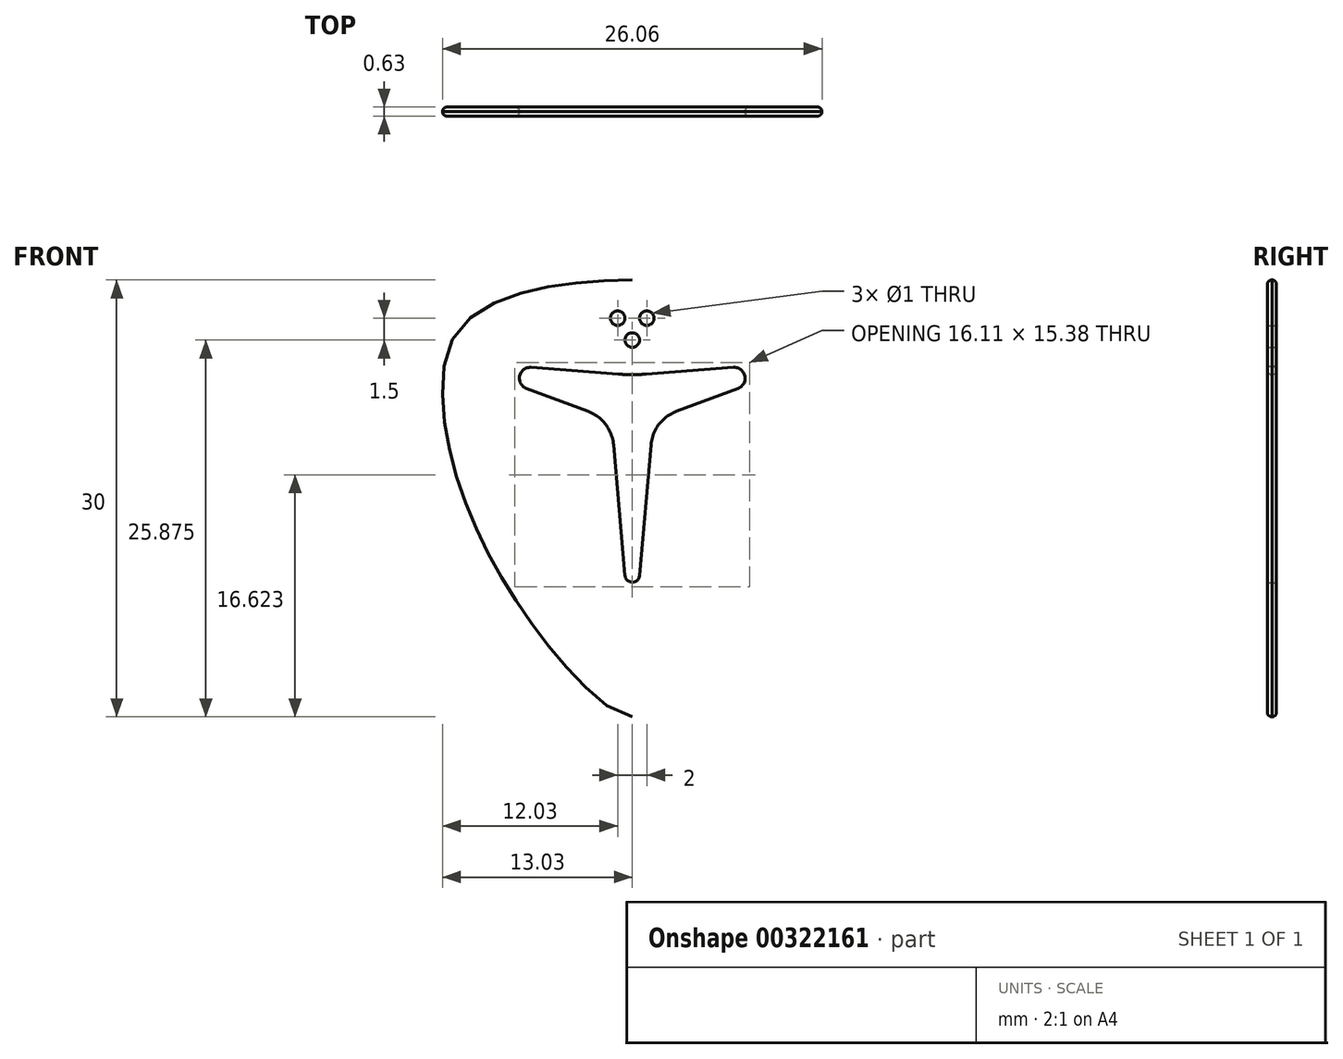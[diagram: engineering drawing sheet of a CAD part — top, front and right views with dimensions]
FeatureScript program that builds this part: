
annotation { "Feature Type Name" : "Feature", "Feature Type Description" : "" }
export const myFeature = defineFeature(function(context is Context, id is Id, definition is map)
    precondition{}
    {
        {
            var Q0;
            Q0=qCreatedBy(makeId("Front.planeOp"),FACE);
            var sketch = newSketch(context, id + "F0", { "sketchPlane" : qUnion([Q0])});
            skLineSegment(sketch, "E0", {"start": v(0, 0) * mm, "end": v(0, 6.75) * mm, "construction": true});
            skLineSegment(sketch, "E1", {"start": v(0, 0) * mm, "end": v(0, -23.25) * mm, "construction": true});
            skLineSegment(sketch, "E2", {"start": v(0, 0) * mm, "end": v(13, 0) * mm, "construction": true});
            skFitSpline(sketch, "E3", {"points": [v(0, -23.25) * mm, v(9.5, -12.75) * mm, v(13, 0) * mm, v(11, 4.25) * mm, v(0, 6.75) * mm], "startDerivative": vector(20.6, 0) * mm, "endDerivative": vector(-57.72, 0) * mm});
            skFitSpline(sketch, "E4.MirrorCS", {"points": [v(0, -23.25) * mm, v(-9.5, -12.75) * mm, v(-13, 0) * mm, v(-11, 4.25) * mm, v(0, 6.75) * mm], "startDerivative": vector(-20.6, 0) * mm, "endDerivative": vector(57.72, 0) * mm});
            skArc(sketch, "E5", {"start": v(7.26, -0.7) * mm, "mid": v(7.73, 0.16) * mm, "end": v(6.94, 0.75) * mm});
            skLineSegment(sketch, "E6", {"start": v(7.26, -0.7) * mm, "end": v(3.04, -2.27) * mm});
            skArc(sketch, "E7", {"start": v(3.04, -2.27) * mm, "mid": v(1.83, -3.17) * mm, "end": v(1.28, -4.58) * mm});
            skLineSegment(sketch, "E8", {"start": v(0.5, -13.54) * mm, "end": v(1.28, -4.58) * mm});
            skArc(sketch, "E9", {"start": v(0, -14) * mm, "mid": v(0.34, -13.87) * mm, "end": v(0.5, -13.54) * mm});
            skArc(sketch, "E10.MirrorCS", {"start": v(0, -14) * mm, "mid": v(-0.34, -13.87) * mm, "end": v(-0.5, -13.54) * mm});
            skLineSegment(sketch, "E11.MirrorCS", {"start": v(-0.5, -13.54) * mm, "end": v(-1.28, -4.58) * mm});
            skArc(sketch, "E12.MirrorCS", {"start": v(-3.04, -2.27) * mm, "mid": v(-1.83, -3.17) * mm, "end": v(-1.28, -4.58) * mm});
            skLineSegment(sketch, "E13.MirrorCS", {"start": v(-7.26, -0.7) * mm, "end": v(-3.04, -2.27) * mm});
            skArc(sketch, "E14.MirrorCS", {"start": v(-7.26, -0.7) * mm, "mid": v(-7.73, 0.16) * mm, "end": v(-6.94, 0.75) * mm});
            skLineSegment(sketch, "E15", {"start": v(6.94, 0.75) * mm, "end": v(0.96, 0.29) * mm});
            skArc(sketch, "E16", {"start": v(0, 0.25) * mm, "mid": v(0.48, 0.26) * mm, "end": v(0.96, 0.29) * mm});
            skArc(sketch, "E17.MirrorCS", {"start": v(0, 0.25) * mm, "mid": v(-0.48, 0.26) * mm, "end": v(-0.96, 0.29) * mm});
            skLineSegment(sketch, "E18.MirrorCS", {"start": v(-6.94, 0.75) * mm, "end": v(-0.96, 0.29) * mm});
            skLineSegment(sketch, "E19", {"start": v(0, 4.12) * mm, "end": v(1, 4.12) * mm});
            skCircle(sketch, "E20", {"center": v(1, 4.12) * mm, "radius": 0.5 * mm});
            skCircle(sketch, "E21", {"center": v(0, 2.62) * mm, "radius": 0.5 * mm});
            skPoint(sketch, "E22", {"position": v(0, 3.38) * mm});
            skLineSegment(sketch, "E23.MirrorCS", {"start": v(0, 4.12) * mm, "end": v(-1, 4.12) * mm});
            skCircle(sketch, "E24.MirrorC", {"center": v(-1, 4.12) * mm, "radius": 0.5 * mm});
            skSolve(sketch);
        }
        {
            var Q0;
            Q0=qSketchRegion(id+"F0",true);
            extrude(context, id + "F1", {"entities" : qUnion([Q0]), "depth" : 0.63 * mm});
        }
        {
            var Q0;
            Q0=makeQuery(id+"F1.opExtrude","CAP_EDGE",EDGE,{"disambiguationData":[OSD([sQuery(id+"F0.wireOp",EDGE,"E5")])],"isStart":false});
            var Q1;
            Q1=makeQuery(id+"F1.opExtrude","CAP_EDGE",EDGE,{"disambiguationData":[OSD([sQuery(id+"F0.wireOp",EDGE,"E7")])],"isStart":true});
            var Q2;
            Q2=makeQuery(id+"F1.opExtrude","CAP_EDGE",EDGE,{"disambiguationData":[OSD([sQuery(id+"F0.wireOp",EDGE,"E9"),sQuery(id+"F0.wireOp",EDGE,"E10.MirrorCS")])],"isStart":false});
            var Q3;
            Q3=makeQuery(id+"F1.opExtrude","CAP_EDGE",EDGE,{"disambiguationData":[OSD([sQuery(id+"F0.wireOp",EDGE,"E14.MirrorCS")])],"isStart":false});
            var Q4;
            Q4=makeQuery(id+"F1.opExtrude","CAP_EDGE",EDGE,{"disambiguationData":[OSD([sQuery(id+"F0.wireOp",EDGE,"E5")])],"isStart":true});
            var Q5;
            Q5=makeQuery(id+"F1.opExtrude","CAP_EDGE",EDGE,{"disambiguationData":[OSD([sQuery(id+"F0.wireOp",EDGE,"E12.MirrorCS")])],"isStart":false});
            var Q6;
            Q6=makeQuery(id+"F1.opExtrude","CAP_EDGE",EDGE,{"disambiguationData":[OSD([sQuery(id+"F0.wireOp",EDGE,"E7")])],"isStart":false});
            var Q7;
            Q7=makeQuery(id+"F1.opExtrude","CAP_EDGE",EDGE,{"disambiguationData":[OSD([sQuery(id+"F0.wireOp",EDGE,"cP70XH3B-hxny-nh1n-TbyW-52Zl4TOD4HrO"),sQuery(id+"F0.wireOp",EDGE,"9cf6c757-e815-40dd-95a7-672993b90d513.MirrorCS")])],"isStart":true});
            var Q8;
            Q8=makeQuery(id+"F1.opExtrude","CAP_EDGE",EDGE,{"disambiguationData":[OSD([sQuery(id+"F0.wireOp",EDGE,"E13.MirrorCS")])],"isStart":false});
            var Q9;
            Q9=makeQuery(id+"F1.opExtrude","CAP_EDGE",EDGE,{"disambiguationData":[OSD([sQuery(id+"F0.wireOp",EDGE,"E12.MirrorCS")])],"isStart":true});
            var Q10;
            Q10=makeQuery(id+"F1.opExtrude","CAP_EDGE",EDGE,{"disambiguationData":[OSD([sQuery(id+"F0.wireOp",EDGE,"cP70XH3B-hxny-nh1n-TbyW-52Zl4TOD4HrO"),sQuery(id+"F0.wireOp",EDGE,"9cf6c757-e815-40dd-95a7-672993b90d513.MirrorCS")])],"isStart":false});
            var Q11;
            Q11=makeQuery(id+"F1.opExtrude","CAP_EDGE",EDGE,{"disambiguationData":[OSD([sQuery(id+"F0.wireOp",EDGE,"E9"),sQuery(id+"F0.wireOp",EDGE,"E10.MirrorCS")])],"isStart":true});
            var Q12;
            Q12=makeQuery(id+"F1.opExtrude","SWEPT_EDGE",EDGE,{"disambiguationData":[OSD([sQuery(id+"F0.wireOp",EDGE,"9cf6c757-e815-40dd-95a7-672993b90d513.MirrorCS"),sQuery(id+"F0.wireOp",EDGE,"E14.MirrorCS")])]});
            var Q13;
            Q13=makeQuery(id+"F1.opExtrude","CAP_EDGE",EDGE,{"disambiguationData":[OSD([sQuery(id+"F0.wireOp",EDGE,"E8")])],"isStart":true});
            var Q14;
            Q14=makeQuery(id+"F1.opExtrude","CAP_EDGE",EDGE,{"disambiguationData":[OSD([sQuery(id+"F0.wireOp",EDGE,"E11.MirrorCS")])],"isStart":false});
            var Q15;
            Q15=makeQuery(id+"F1.opExtrude","SWEPT_EDGE",EDGE,{"disambiguationData":[OSD([sQuery(id+"F0.wireOp",EDGE,"E6"),sQuery(id+"F0.wireOp",EDGE,"E7")])]});
            var Q16;
            Q16=makeQuery(id+"F1.opExtrude","SWEPT_EDGE",EDGE,{"disambiguationData":[OSD([sQuery(id+"F0.wireOp",EDGE,"E8"),sQuery(id+"F0.wireOp",EDGE,"E9")])]});
            var Q17;
            Q17=makeQuery(id+"F1.opExtrude","SWEPT_EDGE",EDGE,{"disambiguationData":[OSD([sQuery(id+"F0.wireOp",EDGE,"E13.MirrorCS"),sQuery(id+"F0.wireOp",EDGE,"E14.MirrorCS")])]});
            var Q18;
            Q18=makeQuery(id+"F1.opExtrude","SWEPT_EDGE",EDGE,{"disambiguationData":[OSD([sQuery(id+"F0.wireOp",EDGE,"E10.MirrorCS"),sQuery(id+"F0.wireOp",EDGE,"E11.MirrorCS")])]});
            var Q19;
            Q19=makeQuery(id+"F1.opExtrude","SWEPT_EDGE",EDGE,{"disambiguationData":[OSD([sQuery(id+"F0.wireOp",EDGE,"E11.MirrorCS"),sQuery(id+"F0.wireOp",EDGE,"E12.MirrorCS")])]});
            var Q20;
            Q20=makeQuery(id+"F1.opExtrude","SWEPT_EDGE",EDGE,{"disambiguationData":[OSD([sQuery(id+"F0.wireOp",EDGE,"E5"),sQuery(id+"F0.wireOp",EDGE,"E6")])]});
            var Q21;
            Q21=makeQuery(id+"F1.opExtrude","CAP_EDGE",EDGE,{"disambiguationData":[OSD([sQuery(id+"F0.wireOp",EDGE,"E14.MirrorCS")])],"isStart":true});
            var Q22;
            Q22=makeQuery(id+"F1.opExtrude","SWEPT_EDGE",EDGE,{"disambiguationData":[OSD([sQuery(id+"F0.wireOp",EDGE,"E12.MirrorCS"),sQuery(id+"F0.wireOp",EDGE,"E13.MirrorCS")])]});
            var Q23;
            Q23=makeQuery(id+"F1.opExtrude","CAP_EDGE",EDGE,{"disambiguationData":[OSD([sQuery(id+"F0.wireOp",EDGE,"E8")])],"isStart":false});
            var Q24;
            Q24=makeQuery(id+"F1.opExtrude","SWEPT_EDGE",EDGE,{"disambiguationData":[OSD([sQuery(id+"F0.wireOp",EDGE,"cP70XH3B-hxny-nh1n-TbyW-52Zl4TOD4HrO"),sQuery(id+"F0.wireOp",EDGE,"E5")])]});
            var Q25;
            Q25=makeQuery(id+"F1.opExtrude","CAP_EDGE",EDGE,{"disambiguationData":[OSD([sQuery(id+"F0.wireOp",EDGE,"E6")])],"isStart":false});
            var Q26;
            Q26=makeQuery(id+"F1.opExtrude","CAP_EDGE",EDGE,{"disambiguationData":[OSD([sQuery(id+"F0.wireOp",EDGE,"E11.MirrorCS")])],"isStart":true});
            var Q27;
            Q27=makeQuery(id+"F1.opExtrude","SWEPT_EDGE",EDGE,{"disambiguationData":[OSD([sQuery(id+"F0.wireOp",EDGE,"E7"),sQuery(id+"F0.wireOp",EDGE,"E8")])]});
            var Q28;
            Q28=makeQuery(id+"F1.opExtrude","CAP_EDGE",EDGE,{"disambiguationData":[OSD([sQuery(id+"F0.wireOp",EDGE,"E6")])],"isStart":true});
            var Q29;
            Q29=makeQuery(id+"F1.opExtrude","CAP_EDGE",EDGE,{"disambiguationData":[OSD([sQuery(id+"F0.wireOp",EDGE,"E13.MirrorCS")])],"isStart":true});
            var Q30;
            Q30=makeQuery(id+"F1.opExtrude","CAP_EDGE",EDGE,{"disambiguationData":[OSD([sQuery(id+"F0.wireOp",EDGE,"E18.MirrorCS")])],"isStart":false});
            var Q31;
            Q31=makeQuery(id+"F1.opExtrude","CAP_EDGE",EDGE,{"disambiguationData":[OSD([sQuery(id+"F0.wireOp",EDGE,"E18.MirrorCS")])],"isStart":true});
            var Q32;
            Q32=makeQuery(id+"F1.opExtrude","CAP_EDGE",EDGE,{"disambiguationData":[OSD([sQuery(id+"F0.wireOp",EDGE,"E16"),sQuery(id+"F0.wireOp",EDGE,"E17.MirrorCS")])],"isStart":false});
            fillet(context, id + "F2", {"entities" : qUnion([Q0, Q1, Q2, Q3, Q4, Q5, Q6, Q7, Q8, Q9, Q10, Q11, Q12, Q13, Q14, Q15, Q16, Q17, Q18, Q19, Q20, Q21, Q22, Q23, Q24, Q25, Q26, Q27, Q28, Q29, Q30, Q31, Q32]), "radius" : (0.63 / 2) * mm, "tangentPropagation" : true, "allowEdgeOverflow" : false});
        }
        {
            var Q0;
            Q0=makeQuery(id+"F1.opExtrude","CAP_EDGE",EDGE,{"disambiguationData":[OSD([sQuery(id+"F0.wireOp",EDGE,"E4.MirrorCS")])],"isStart":false});
            var Q1;
            Q1=makeQuery(id+"F1.opExtrude","CAP_EDGE",EDGE,{"disambiguationData":[OSD([sQuery(id+"F0.wireOp",EDGE,"E3")])],"isStart":false});
            var Q2;
            Q2=makeQuery(id+"F1.opExtrude","CAP_EDGE",EDGE,{"disambiguationData":[OSD([sQuery(id+"F0.wireOp",EDGE,"E4.MirrorCS")])],"isStart":true});
            var Q3;
            Q3=makeQuery(id+"F1.opExtrude","CAP_EDGE",EDGE,{"disambiguationData":[OSD([sQuery(id+"F0.wireOp",EDGE,"E3")])],"isStart":true});
            fillet(context, id + "F3", {"entities" : qUnion([Q0, Q1, Q2, Q3]), "radius" : 0.63 / 2 * mm, "tangentPropagation" : true, "allowEdgeOverflow" : false});
        }
    });
